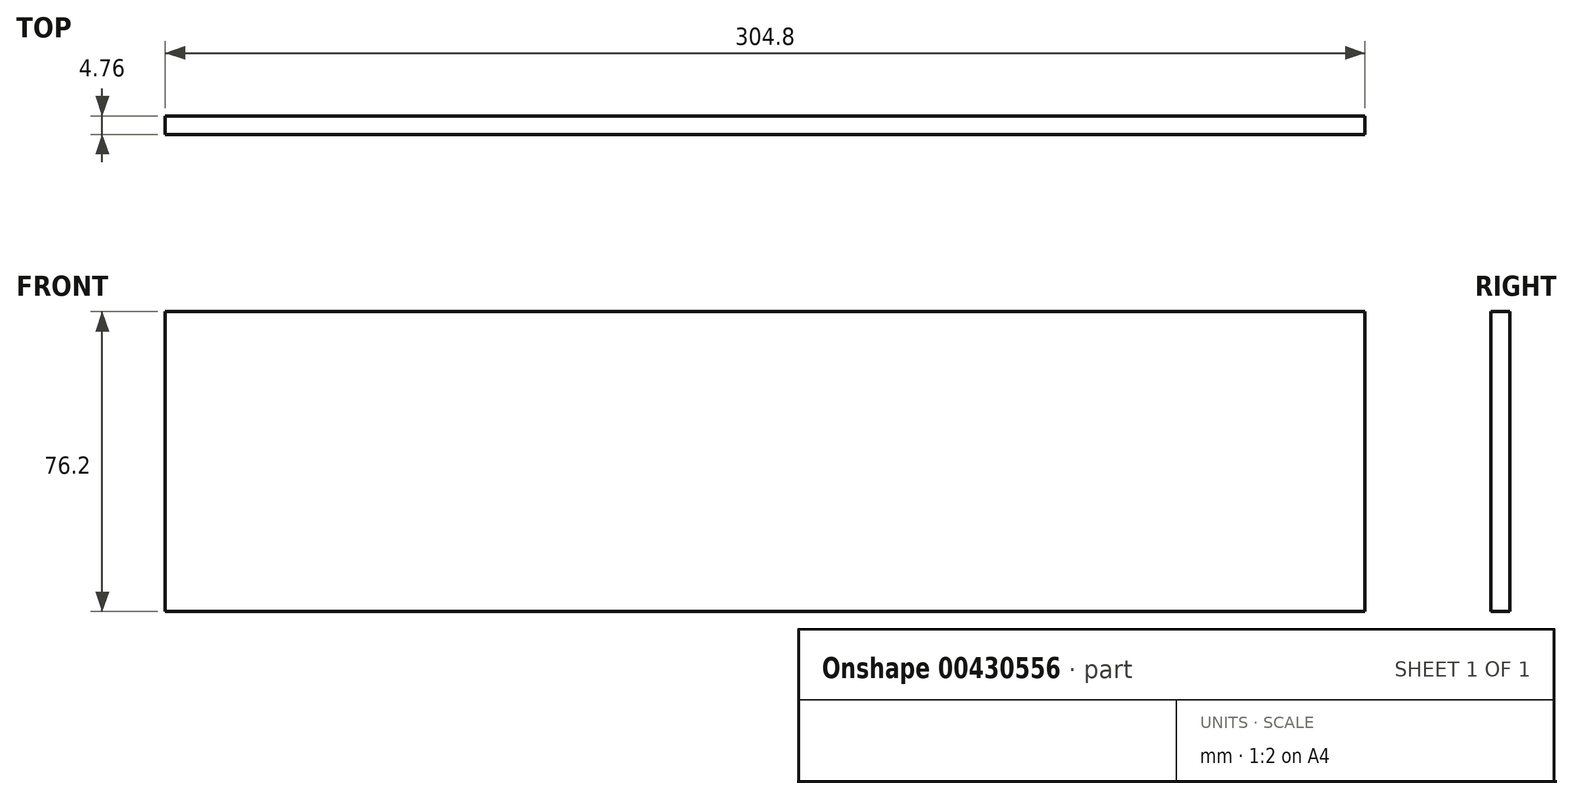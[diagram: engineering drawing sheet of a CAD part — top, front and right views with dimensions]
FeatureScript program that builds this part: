
annotation { "Feature Type Name" : "Feature", "Feature Type Description" : "" }
export const myFeature = defineFeature(function(context is Context, id is Id, definition is map)
    precondition{}
    {
        {
            var Q0;
            Q0=qCreatedBy(makeId("Front.planeOp"),FACE);
            var sketch = newSketch(context, id + "F0", { "sketchPlane" : qUnion([Q0])});
            skLineSegment(sketch, "E0.bottom", {"start": v(-153.81, 42.93) * mm, "end": v(150.99, 42.93) * mm});
            skLineSegment(sketch, "E0.top", {"start": v(-153.81, -33.27) * mm, "end": v(150.99, -33.27) * mm});
            skLineSegment(sketch, "E0.left", {"start": v(-153.81, 42.93) * mm, "end": v(-153.81, -33.27) * mm});
            skLineSegment(sketch, "E0.right", {"start": v(150.99, 42.93) * mm, "end": v(150.99, -33.27) * mm});
            skSolve(sketch);
        }
        {
            var Q0;
            Q0=makeQuery(id+"F0.imprint","IMPRINT",FACE,{"disambiguationData":[TD([[makeQuery(id+"F0.imprint","IMPRINT",EDGE,{"derivedFrom":sQuery(id+"F0.wireOp",EDGE,"E0.bottom")}),-1.0]])]});
            extrude(context, id + "F1", {"entities" : qUnion([Q0]), "depth" : 4.76 * mm});
        }
    });
